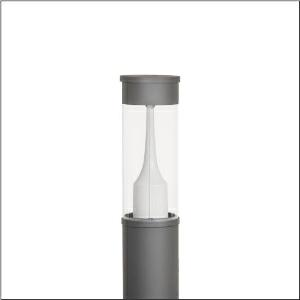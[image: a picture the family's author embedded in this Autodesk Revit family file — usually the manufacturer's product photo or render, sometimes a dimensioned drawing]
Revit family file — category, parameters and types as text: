
# Revit family: city-light_120_iq___p1_0a_5xa5285nf14h_00f5
name_source: partatom
category: Lighting Fixtures
units: mm (PartAtom-declared; Revit-internal decimal feet)

## family parameters
Cut with Voids When Loaded = No
Host = Face
Light Source = No
Part Type = Normal
Room Calculation Point = No
Round Connector Dimension = Use Diameter
Shared = No

## types (1)
- --- (1 x LED, 1510 lm, 11.8 W, 2700K)
    Apparent Load = 12 VA
    CIE Flux Codes = 32 61 90 93 100
    Color Rendering = 70
    Color Temperature = 2700K
    Default Elevation = 1800 mm
    Description = City-Light 120 iQ, bollard luminaire, Module 540 iQ-SR, primary light control with 3 zone facetted reflector, of plastic, silver coated, highly specular, structured, primary optical cover: cover, of PMMA, transparent, partly coated, light distribution: P1.0a, primary light characteristic: strongly asymmetric, LED, High Power LED, rated luminous flux: 1.510lm, luminous efficacy: 128lm/W, light colour: 727, colour temperature: 2700K, control gear: ECG iQ, control: presetting dimming logarithmic, Street-Remote, Auto-Match, Temp-Guard, Lumen-Switch, Night-Set, Smart-Wire, Light-Fading, Desk-Remote (wireless, voltage-free reading and setting of iQ features in the workshop via application-optimized NFC function/RFID function), optimised constant luminous flux control (CLO 2.0), with terminal, 6-pole, max. 2.5mm², mains connection: 230..240V, AC, 50/60Hz, start of lifetime: 12W, end of service life: 12W, reduction: 6W, luminaire housing, cylindrical, of extruded aluminium section, coated, Siteco® metallic grey (DB 702S), length: 1.200mm, diameter: 200mm, Module 540 iQ-SR, traffic white (RAL 9016), equipment: standard, protection rating (complete): IP54, insulation class (complete): insulation class II (safety insulation), certification: CE, ENEC, VDE, packaging unit: 1 piece

Light Distribution: P1.0a
    Height = 500 mm
    Lamp = 1 x LED
    Lamp Light Flux = 1510 lm
    Lamp Power = 11.8 W
    Lamp count = 1
    Length = 200 mm  [stored 0.656168 ft]
    Luminous efficacy = 128 lm/W
    Manufacturer = Siteco
    ModVariant = No
    Model = 5XA5285NF14H
    Mounting Place = Floor
    Mounting Type = Freestanding
    Number of Poles = 1
    OnlyDefault = Yes
    Power Factor = 1
    Product Name = City-Light 120 iQ | P1.0a
    Product group = bollard luminaire
    ProductGroupID = 1304
    Protection Class = Protection class II
    Protection Degree = IP 54
    RLX_Detail_Level = 1
    RLX_Emergency_Light_Flux = 0 lm
    RLX_Emergency_Type = 0
    RLX_Emergency_Type_DB = No
    RlxData = <blob elided: 52377 chars, md5=dbd687fb>
    Socket = socket
    Standby Power = 0 W
    System Light Flux = 1510 lm
    System Power = 12 W
    Type Comments = factory setting: luminous flux: 100 % | dim-lin: 254 | 472 mA
    Type Image = l_1006922.jpg
    URL = http://relux.com
    VarID = @adj_085487
    Voltage = 0 V
    Weight = 0.00 kg
    Width = 0 mm  [stored 0 ft]

note: [stored X ft] marks values corroborated as IEEE doubles in the binary element streams (Revit-internal decimal feet)

## geometry (parser evidence)
native form markers: Blend x4, Sweep x10
no freeform markers — native parametric forms only
